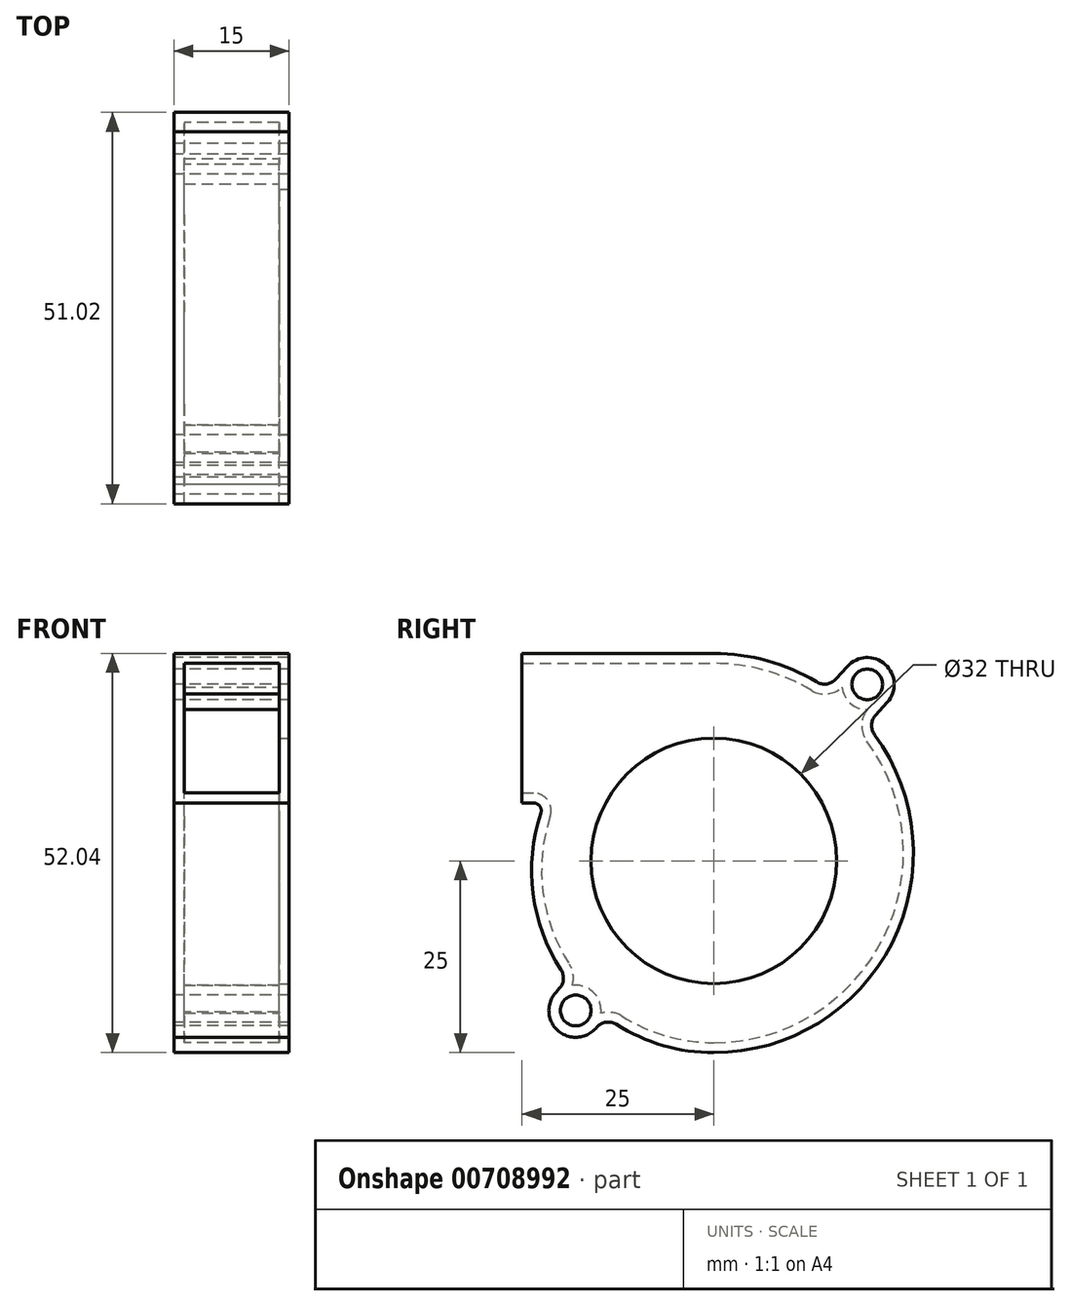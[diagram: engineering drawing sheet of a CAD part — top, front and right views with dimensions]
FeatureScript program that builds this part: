
annotation { "Feature Type Name" : "Feature", "Feature Type Description" : "" }
export const myFeature = defineFeature(function(context is Context, id is Id, definition is map)
    precondition{}
    {
        {
            var Q0;
            Q0=qCreatedBy(makeId("Right.planeOp"),FACE);
            var sketch = newSketch(context, id + "F0", { "sketchPlane" : qUnion([Q0])});
            skCircle(sketch, "E0", {"center": v(0, 0) * mm, "radius": 12 * mm});
            skCircle(sketch, "E1", {"center": v(20, 23) * mm, "radius": 2 * mm});
            skCircle(sketch, "E2", {"center": v(-18, -19.5) * mm, "radius": 2 * mm});
            skLineSegment(sketch, "E3", {"start": v(-25, 27.04) * mm, "end": v(-25, 7.54) * mm});
            skLineSegment(sketch, "E4", {"start": v(26, 45.4) * mm, "end": v(26, -37.85) * mm, "construction": true});
            skCircle(sketch, "E5", {"center": v(0, 0) * mm, "radius": 16 * mm});
            skLineSegment(sketch, "E6", {"start": v(-25, 27.04) * mm, "end": v(65.28, 27.04) * mm, "construction": true});
            skLineSegment(sketch, "E7", {"start": v(-25, 27.04) * mm, "end": v(0, 27.04) * mm});
            skArc(sketch, "E8", {"start": v(22.6, 20.66) * mm, "mid": v(22.34, 25.6) * mm, "end": v(17.4, 25.34) * mm});
            skArc(sketch, "E9", {"start": v(-20.6, -17.16) * mm, "mid": v(-20.34, -22.1) * mm, "end": v(-15.4, -21.84) * mm});
            skArc(sketch, "E10", {"start": v(26, 0) * mm, "mid": v(24.88, 8.65) * mm, "end": v(20.95, 16.45) * mm});
            skArc(sketch, "E11", {"start": v(0, -25) * mm, "mid": v(18.03, -17.74) * mm, "end": v(26, 0) * mm});
            skArc(sketch, "E12", {"start": v(-22.55, 6.23) * mm, "mid": v(-23.56, -4.28) * mm, "end": v(-19.92, -14.19) * mm});
            skLineSegment(sketch, "E13", {"start": v(-25, 7.54) * mm, "end": v(-23.5, 7.54) * mm});
            skPoint(sketch, "E14.visualSharp", {"position": v(-22.07, 7.54) * mm});
            skArc(sketch, "E14.filletArc", {"start": v(-22.55, 6.23) * mm, "mid": v(-22.69, 7.13) * mm, "end": v(-23.5, 7.54) * mm});
            skLineSegment(sketch, "E15", {"start": v(-20.6, -17.16) * mm, "end": v(-20.11, -16.62) * mm});
            skLineSegment(sketch, "E16", {"start": v(-15.4, -21.84) * mm, "end": v(-15.25, -21.68) * mm});
            skLineSegment(sketch, "E17", {"start": v(17.4, 25.34) * mm, "end": v(15.92, 23.7) * mm});
            skLineSegment(sketch, "E18", {"start": v(22.6, 20.66) * mm, "end": v(21.08, 18.97) * mm});
            skArc(sketch, "E19.trimOffspring", {"start": v(-12.7, -21.32) * mm, "mid": v(-6.6, -24.06) * mm, "end": v(0, -25) * mm});
            skArc(sketch, "E20.trimOffspring", {"start": v(13.4, 23.32) * mm, "mid": v(6.95, 26.1) * mm, "end": v(0, 27.04) * mm});
            skPoint(sketch, "E21.visualSharp", {"position": v(14.78, 22.44) * mm});
            skArc(sketch, "E21.filletArc", {"start": v(13.4, 23.32) * mm, "mid": v(14.73, 23.06) * mm, "end": v(15.92, 23.7) * mm});
            skPoint(sketch, "E22.visualSharp", {"position": v(19.95, 17.72) * mm});
            skArc(sketch, "E22.filletArc", {"start": v(21.08, 18.97) * mm, "mid": v(20.57, 17.73) * mm, "end": v(20.95, 16.45) * mm});
            skPoint(sketch, "E23.visualSharp", {"position": v(-19.05, -15.44) * mm});
            skArc(sketch, "E23.filletArc", {"start": v(-20.11, -16.62) * mm, "mid": v(-19.6, -15.43) * mm, "end": v(-19.92, -14.19) * mm});
            skPoint(sketch, "E24.visualSharp", {"position": v(-14.08, -20.38) * mm});
            skArc(sketch, "E24.filletArc", {"start": v(-12.7, -21.32) * mm, "mid": v(-14.04, -21.03) * mm, "end": v(-15.25, -21.68) * mm});
            skSolve(sketch);
        }
        {
            var Q0;
            Q0=makeQuery(id+"F0.imprint","IMPRINT",FACE,{"disambiguationData":[TD([[makeQuery(id+"F0.imprint","IMPRINT",EDGE,{"derivedFrom":sQuery(id+"F0.wireOp",EDGE,"E1")}),-1.0]])]});
            var Q1;
            Q1=makeQuery(id+"F0.imprint","IMPRINT",FACE,{"disambiguationData":[TD([[makeQuery(id+"F0.imprint","IMPRINT",EDGE,{"derivedFrom":sQuery(id+"F0.wireOp",EDGE,"E0")}),-1.0]])]});
            var Q2;
            Q2=makeQuery(id+"F0.imprint","IMPRINT",FACE,{"disambiguationData":[TD([[makeQuery(id+"F0.imprint","IMPRINT",EDGE,{"derivedFrom":sQuery(id+"F0.wireOp",EDGE,"E0")}),1.0]])]});
            extrude(context, id + "F1", {"entities" : qUnion([Q0, Q1, Q2]), "depth" : 15 * mm});
        }
        {
            var Q0;
            Q0=makeQuery(id+"F1.opExtrude","SWEPT_FACE",FACE,{"disambiguationData":[OSD([sQuery(id+"F0.wireOp",EDGE,"E3")])]});
            shell(context, id + "F2", {"entities" : qUnion([Q0]), "thickness" : 1.3 * mm});
        }
        {
            var Q0;
            Q0=makeQuery(id+"F1.opExtrude","CAP_FACE",FACE,{"disambiguationData":[OSD([sQuery(id+"F0.wireOp",EDGE,"E1"),sQuery(id+"F0.wireOp",EDGE,"E2"),sQuery(id+"F0.wireOp",EDGE,"E3"),sQuery(id+"F0.wireOp",EDGE,"E7"),sQuery(id+"F0.wireOp",EDGE,"E8"),sQuery(id+"F0.wireOp",EDGE,"E9"),sQuery(id+"F0.wireOp",EDGE,"E10"),sQuery(id+"F0.wireOp",EDGE,"E11"),sQuery(id+"F0.wireOp",EDGE,"E12"),sQuery(id+"F0.wireOp",EDGE,"E13"),sQuery(id+"F0.wireOp",EDGE,"E14.filletArc"),sQuery(id+"F0.wireOp",EDGE,"E15"),sQuery(id+"F0.wireOp",EDGE,"E16"),sQuery(id+"F0.wireOp",EDGE,"E17"),sQuery(id+"F0.wireOp",EDGE,"E18"),sQuery(id+"F0.wireOp",EDGE,"E19.trimOffspring"),sQuery(id+"F0.wireOp",EDGE,"E20.trimOffspring"),sQuery(id+"F0.wireOp",EDGE,"E21.filletArc"),sQuery(id+"F0.wireOp",EDGE,"E22.filletArc"),sQuery(id+"F0.wireOp",EDGE,"E23.filletArc"),sQuery(id+"F0.wireOp",EDGE,"E24.filletArc")])],"isStart":false});
            var sketch = newSketch(context, id + "F3", { "sketchPlane" : qUnion([Q0])});
            skCircle(sketch, "E25.0", {"center": v(0, 0) * mm, "radius": 16 * mm});
            skSolve(sketch);
        }
        {
            var Q0;
            Q0=qSketchRegion(id+"F3",true);
            var Q1;
            {var subQ0=sQuery(id+"F0.wireOp",EDGE,"E24.filletArc");var subQ1=sQuery(id+"F0.wireOp",EDGE,"E23.filletArc");var subQ2=sQuery(id+"F0.wireOp",EDGE,"E22.filletArc");var subQ3=sQuery(id+"F0.wireOp",EDGE,"E21.filletArc");var subQ4=sQuery(id+"F0.wireOp",EDGE,"E20.trimOffspring");var subQ5=sQuery(id+"F0.wireOp",EDGE,"E19.trimOffspring");var subQ6=sQuery(id+"F0.wireOp",EDGE,"E18");var subQ7=sQuery(id+"F0.wireOp",EDGE,"E17");var subQ8=sQuery(id+"F0.wireOp",EDGE,"E16");var subQ9=sQuery(id+"F0.wireOp",EDGE,"E15");var subQ10=sQuery(id+"F0.wireOp",EDGE,"E14.filletArc");var subQ11=sQuery(id+"F0.wireOp",EDGE,"E13");var subQ12=sQuery(id+"F0.wireOp",EDGE,"E12");var subQ13=sQuery(id+"F0.wireOp",EDGE,"E11");var subQ14=sQuery(id+"F0.wireOp",EDGE,"E10");var subQ15=sQuery(id+"F0.wireOp",EDGE,"E9");var subQ16=sQuery(id+"F0.wireOp",EDGE,"E8");var subQ17=sQuery(id+"F0.wireOp",EDGE,"E7");var subQ18=sQuery(id+"F0.wireOp",EDGE,"E3");var subQ19=sQuery(id+"F0.wireOp",EDGE,"E2");var subQ20=sQuery(id+"F0.wireOp",EDGE,"E1");Q1=makeQuery(id+"F2.opShell","OFFSET_FACE",FACE,{"disambiguationData":[OSD([subQ20,subQ19,subQ18,subQ17,subQ16,subQ15,subQ14,subQ13,subQ12,subQ11,subQ10,subQ9,subQ8,subQ7,subQ6,subQ5,subQ4,subQ3,subQ2,subQ1,subQ0]),TDD([makeQuery(id+"F1.opExtrude","CAP_FACE",FACE,{"disambiguationData":[OSD([subQ20,subQ19,subQ18,subQ17,subQ16,subQ15,subQ14,subQ13,subQ12,subQ11,subQ10,subQ9,subQ8,subQ7,subQ6,subQ5,subQ4,subQ3,subQ2,subQ1,subQ0])],"isStart":true})])]});}
            extrude(context, id + "F4", {"entities" : qUnion([Q0]), "operationType" : NewBodyOperationType.REMOVE, "endBound" : BoundingType.UP_TO_SURFACE, "oppositeDirection" : true, "depth" : 25 * mm, "endBoundEntityFace" : qUnion([Q1]), "offsetDistance" : 25 * mm});
        }
    });
